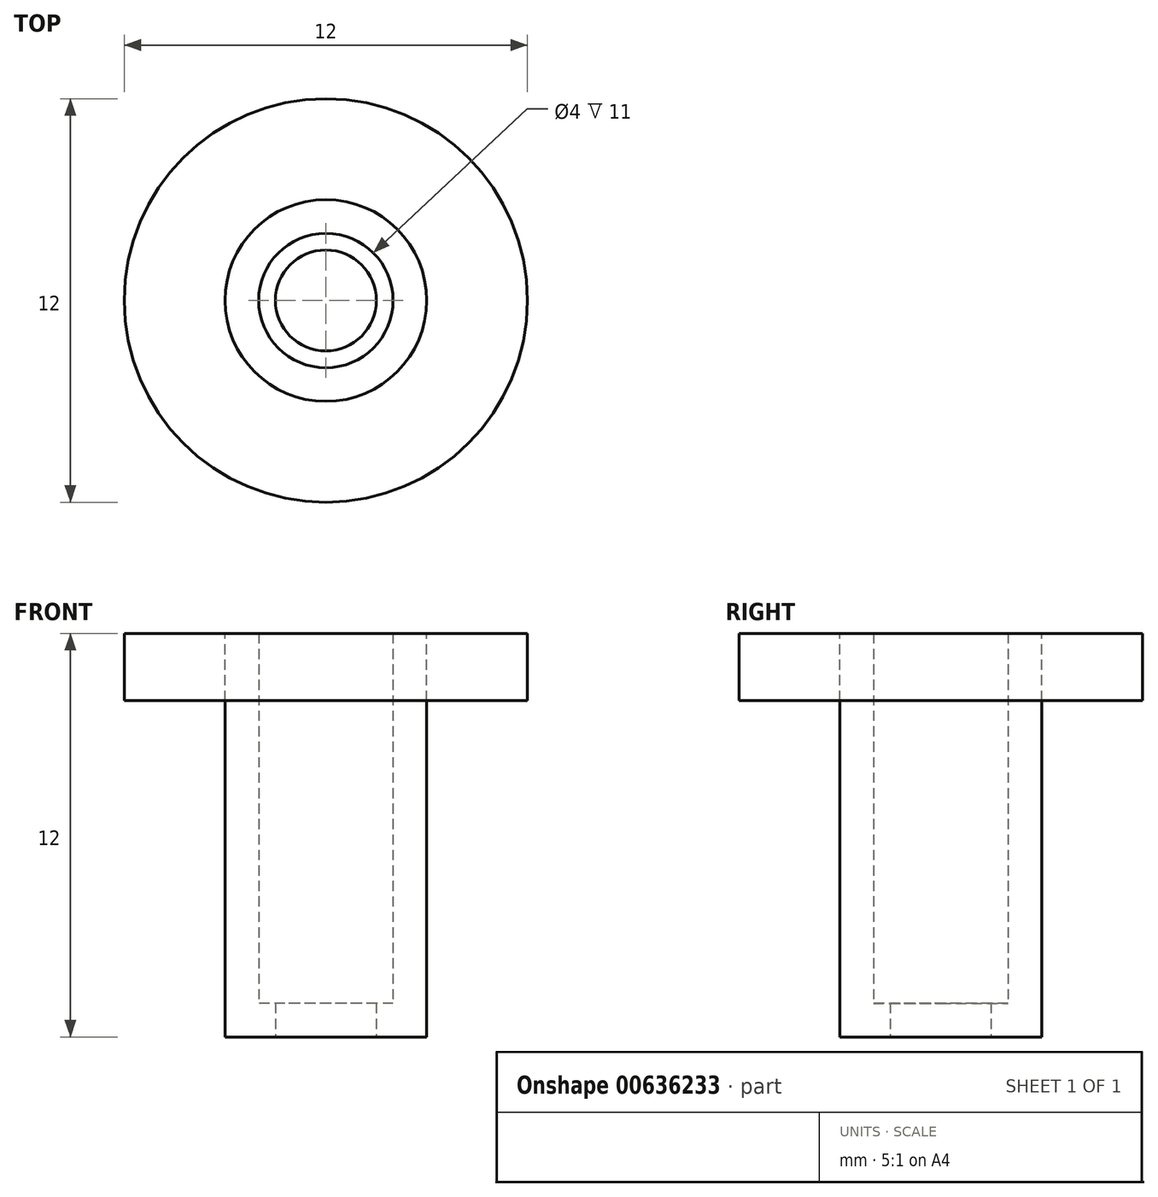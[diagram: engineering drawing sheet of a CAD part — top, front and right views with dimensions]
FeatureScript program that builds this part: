
annotation { "Feature Type Name" : "Feature", "Feature Type Description" : "" }
export const myFeature = defineFeature(function(context is Context, id is Id, definition is map)
    precondition{}
    {
        {
            var Q0;
            Q0=qCreatedBy(makeId("Top.planeOp"),FACE);
            var sketch = newSketch(context, id + "F0", { "sketchPlane" : qUnion([Q0])});
            skCircle(sketch, "E0", {"center": v(0, 0) * mm, "radius": 3 * mm});
            skCircle(sketch, "E1", {"center": v(0, 0) * mm, "radius": 2 * mm});
            skCircle(sketch, "E2", {"center": v(0, 0) * mm, "radius": 1.5 * mm});
            skSolve(sketch);
        }
        {
            var Q0;
            Q0=makeQuery(id+"F0.imprint","IMPRINT",FACE,{"disambiguationData":[TD([[makeQuery(id+"F0.imprint","IMPRINT",EDGE,{"derivedFrom":sQuery(id+"F0.wireOp",EDGE,"E0")}),1.0]])]});
            extrude(context, id + "F1", {"entities" : qUnion([Q0]), "depth" : 12 * mm, "offsetDistance" : 25 * mm});
        }
        {
            var Q0;
            Q0=makeQuery(id+"F0.imprint","IMPRINT",FACE,{"disambiguationData":[TD([[makeQuery(id+"F0.imprint","IMPRINT",EDGE,{"derivedFrom":sQuery(id+"F0.wireOp",EDGE,"E1")}),1.0]])]});
            extrude(context, id + "F2", {"entities" : qUnion([Q0]), "operationType" : NewBodyOperationType.ADD, "depth" : 1 * mm, "offsetDistance" : 25 * mm});
        }
        {
            var Q0;
            Q0=makeQuery(id+"F1.opExtrude","CAP_FACE",FACE,{"disambiguationData":[OSD([sQuery(id+"F0.wireOp",EDGE,"E0"),sQuery(id+"F0.wireOp",EDGE,"E1")])],"isStart":false});
            var sketch = newSketch(context, id + "F3", { "sketchPlane" : qUnion([Q0])});
            skCircle(sketch, "E3", {"center": v(0, 0) * mm, "radius": 6 * mm});
            skSolve(sketch);
        }
        {
            var Q0;
            Q0=makeQuery(id+"F3.imprint","IMPRINT",FACE,{"disambiguationData":[TD([[makeQuery(id+"F3.imprint","IMPRINT",EDGE,{"derivedFrom":sQuery(id+"F3.wireOp",EDGE,"E3")}),1.0]])]});
            extrude(context, id + "F4", {"entities" : qUnion([Q0]), "oppositeDirection" : true, "depth" : 2 * mm, "offsetDistance" : 25 * mm});
        }
    });
